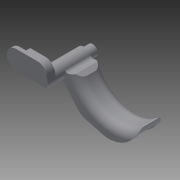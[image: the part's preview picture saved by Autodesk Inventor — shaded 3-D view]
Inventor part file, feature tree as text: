
AUTODESK INVENTOR PART (.ipt)
format: ipt  version: 2014 SP1 (Build 180222100, 222)  size: 2,398,720 bytes
history: native  units: in
note: dims shown in document units (in); Inventor stores cm internally (conversion verified against a paired STEP export)
features: extrude x8, sketch x8, projected_geometry x6, fillet x4, other x1
ambient origin geometry x8: Origin, YZ Plane, XZ Plane, XY Plane, X Axis, Y Axis, Z Axis, Center Point
bodies: Solid1 (feature_tree)
feature tree (27):
  extrude  "Extrusion1"  Depth=0.277in
  extrude  "Extrusion2"  Depth=0.5625in
  extrude  "Extrusion3"  Depth=0.52in TaperAngle=0.0deg
  extrude  "Extrusion4"  Depth=0.128in TaperAngle=0.0deg
  extrude  "Extrusion5"  Depth=0.114in
  extrude  "Extrusion6"  Depth=0.0625in
  fillet  "Fillet1"  Radius=0.061in
  fillet  "Fillet2"  Radius=0.005in
  extrude  "Extrusion7"  Depth=0.05in
  extrude  "Extrusion8"  Depth=0.01in
  fillet  "Fillet3"  Radius=0.0725in
  fillet  "Fillet4"  Radius=0.257in
  sketch  "Sketch1"  dims[d1=1.7767in d5=0.277in]
  other  "Image1"
  sketch  "Sketch2"  dims[d11=0.2115in d20=0.5625in]
  sketch  "Sketch3"  dims[d33=0.375in d34=0.0in d35=0.52in d36=0.0in]
  projected_geometry  "Projected Loop1"
  sketch  "Sketch4"  dims[d37=0.154in d38=0.128in d39=0.0in]
  sketch  "Sketch5"  dims[d40=0.1145in d41=0.0in d42=0.114in]
  projected_geometry  "Projected Loop2"
  sketch  "Sketch6"  dims[d43=0.1085in d44=0.0625in d45=0.061in d46=0.0in d47=0.005in d48=0.0in]
  projected_geometry  "Projected Loop3"
  sketch  "Sketch7"  dims[d49=0.125in d50=0.05in]
  sketch  "Sketch8"  dims[d51=0.0775in d53=0.4245in d54=0.0725in d55=0.257in d56=0.0in d57=0.137in d58=0.257in d59=0.0in d60=0.02in d61=0.01in]
  projected_geometry  "Projected Loop4"
  projected_geometry  "Projected Loop5"
  projected_geometry  "Project Cut Edges1"
